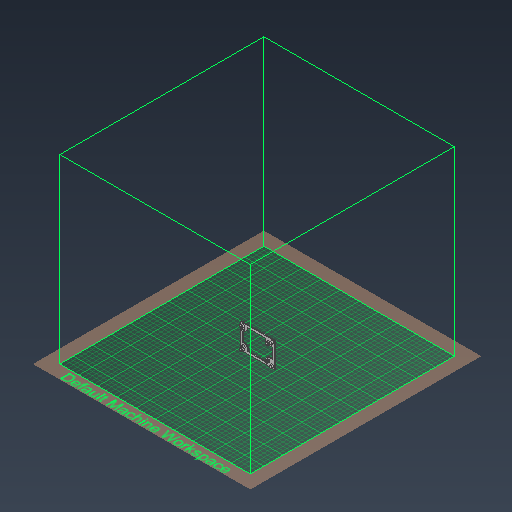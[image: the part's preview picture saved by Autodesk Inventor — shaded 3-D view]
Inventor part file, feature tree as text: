
AUTODESK INVENTOR PART (.ipt)
format: ipt  version: 2021 (Build 250183000, 183)  size: 492,544 bytes
history: native  units: mm
features: extrude x7, sketch x7, fillet x3, projected_geometry x1
ambient origin geometry x8: Origin, YZ Plane, XZ Plane, XY Plane, X Axis, Y Axis, Z Axis, Center Point
bodies: Volumenkörper1 (feature_tree)
feature tree (18):
  extrude  "Extrusion1"  Depth=52.5mm
  extrude  "Extrusion2"  Depth=2.0mm
  sketch  "Skizze5"  dims[d12=17.25mm d13=17.25mm]
  extrude  "Extrusion5"  Depth=7.0mm
  extrude  "Extrusion6"  Depth=34.5mm
  extrude  "Extrusion3"  Depth=17.25mm
  extrude  "Extrusion4"  Depth=55.0mm
  extrude  "Extrusion7"  Depth=3.0mm
  fillet  "Rundung1"  Radius=55.0mm
  fillet  "Rundung2"  Radius=15.0mm
  fillet  "Rundung3"  Radius=5.5mm
  sketch  "Skizze1"  dims[d0=75.0mm d1=52.5mm]
  sketch  "Skizze2"  dims[d2=2.0mm d3=0.0mm d4=7.0mm]
  sketch  "Skizze3"  dims[d5=7.0mm d6=7.0mm]
  sketch  "Skizze4"  dims[d7=7.0mm d8=34.5mm]
  projected_geometry  "Projizierte Kontur1"
  sketch  "Skizze6"  dims[d14=34.5mm d15=55.0mm]
  sketch  "Skizze7"  dims[d16=31.0mm d17=31.0mm d18=55.0mm d19=15.0mm d20=0.0mm d21=5.5mm d22=5.5mm d23=5.5mm d24=5.5mm d25=4.0mm d26=0.0mm d27=3.2mm d28=3.2mm d29=3.2mm d30=3.2mm d31=4.0mm d32=0.0mm d33=7.0mm d34=7.0mm d35=7.0mm d36=7.0mm d39=65.5mm d40=4.75mm d42=45.5mm d44=65.5mm d45=4.5mm d46=4.5mm d47=4.5mm d48=4.5mm d50=7.0mm d53=7.0mm d56=7.0mm d59=7.0mm d62=4.0mm d63=0.0mm d64=6.0mm d65=0.0mm d66=22.75mm d67=32.75mm d68=32.75mm d69=22.75mm d70=32.75mm d71=22.75mm d72=32.75mm d73=32.75mm d74=22.75mm d75=32.75mm d76=22.75mm d77=5.0mm d78=5.0mm d79=15.0mm d80=15.0mm d83=5.0mm d84=15.0mm d86=17.0mm d87=17.0mm d88=5.0mm d89=5.0mm d93=17.0mm d94=5.0mm d95=17.0mm d96=20.0mm d97=20.0mm d98=5.0mm d99=15.0mm d100=6.0mm d101=0.0mm d102=8.0mm d103=3.5mm d104=6.5mm d105=3.0mm]
